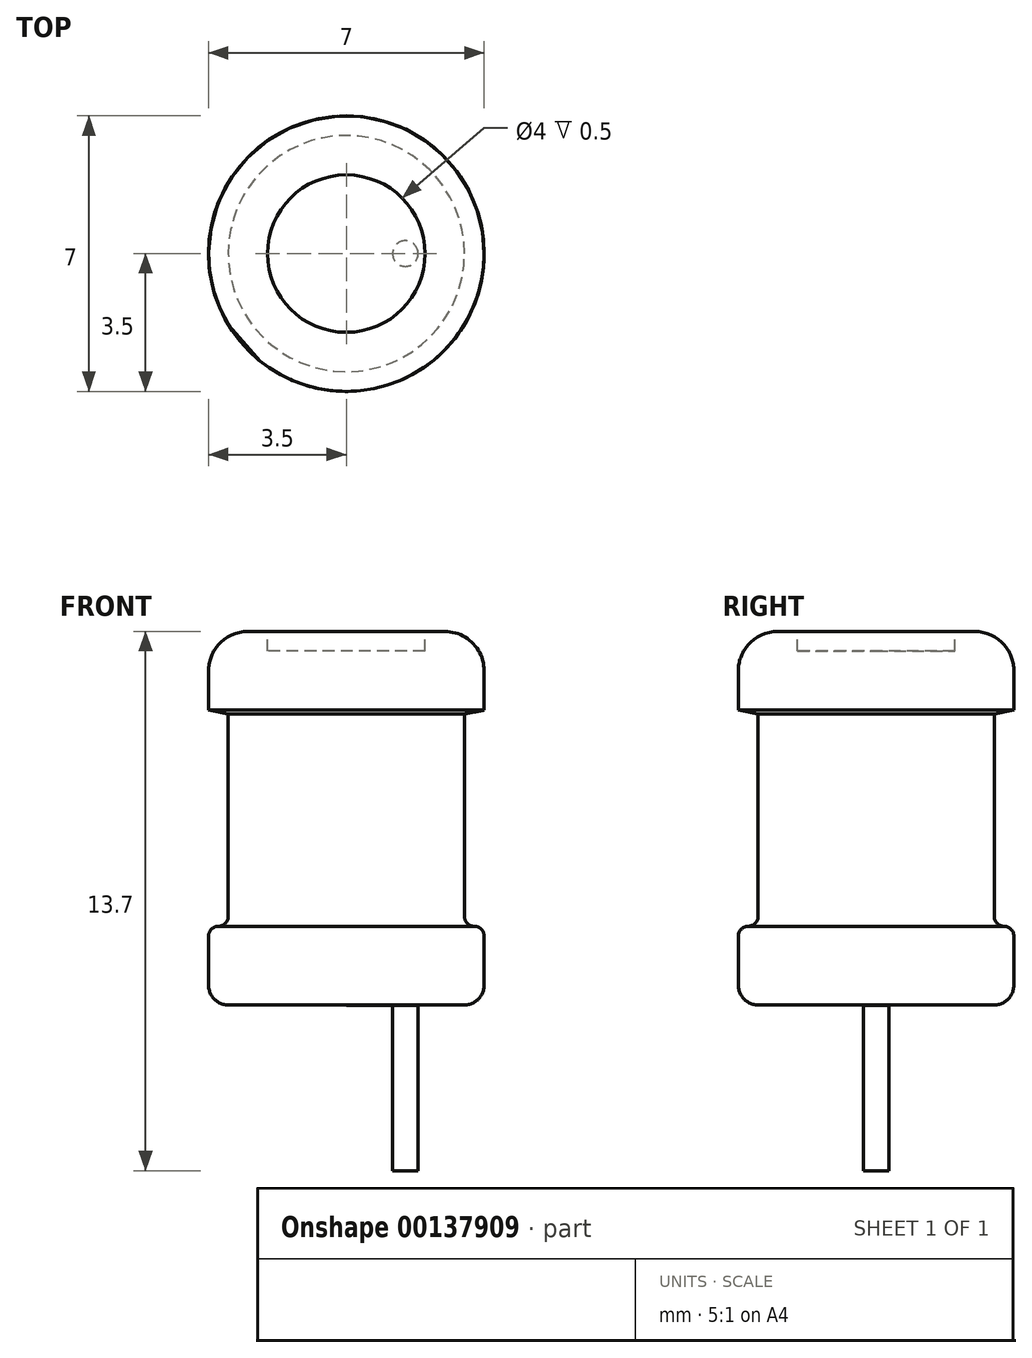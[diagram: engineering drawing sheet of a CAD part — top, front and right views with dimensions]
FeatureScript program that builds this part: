
annotation { "Feature Type Name" : "Feature", "Feature Type Description" : "" }
export const myFeature = defineFeature(function(context is Context, id is Id, definition is map)
    precondition{}
    {
        {
            var Q0;
            Q0=qCreatedBy(makeId("Front.planeOp"),FACE);
            var sketch = newSketch(context, id + "F0", { "sketchPlane" : qUnion([Q0])});
            skLineSegment(sketch, "E0", {"start": v(-2, 9) * mm, "end": v(-2, 9.5) * mm});
            skLineSegment(sketch, "E1", {"start": v(-3.5, 0.5) * mm, "end": v(-3.5, 1.76) * mm});
            skLineSegment(sketch, "E2", {"start": v(-3.25, 2) * mm, "end": v(-3.25, 2) * mm});
            skLineSegment(sketch, "E3", {"start": v(-3, 2.26) * mm, "end": v(-3, 7.4) * mm});
            skLineSegment(sketch, "E4", {"start": v(-3.5, 7.5) * mm, "end": v(-3.5, 8.5) * mm});
            skArc(sketch, "E5.filletArc", {"start": v(-2.5, 9.5) * mm, "mid": v(-3.2, 9.2) * mm, "end": v(-3.5, 8.5) * mm});
            skArc(sketch, "E6.filletArc", {"start": v(-3.25, 2) * mm, "mid": v(-3.43, 1.94) * mm, "end": v(-3.5, 1.76) * mm});
            skArc(sketch, "E7.filletArc", {"start": v(-3.25, 2) * mm, "mid": v(-3.07, 2.08) * mm, "end": v(-3, 2.26) * mm});
            skArc(sketch, "E8.filletArc", {"start": v(-3.5, 0.5) * mm, "mid": v(-3.35, 0.16) * mm, "end": v(-3, 0) * mm});
            skLineSegment(sketch, "E9", {"start": v(-2, 9) * mm, "end": v(0, 9) * mm});
            skLineSegment(sketch, "E10", {"start": v(-3, 0) * mm, "end": v(0, 0) * mm});
            skLineSegment(sketch, "E11", {"start": v(0, 9) * mm, "end": v(0, 0) * mm});
            skLineSegment(sketch, "E12", {"start": v(-2, 9.5) * mm, "end": v(-2.5, 9.5) * mm});
            skLineSegment(sketch, "E13", {"start": v(-3, 7.4) * mm, "end": v(-3.5, 7.5) * mm});
            skSolve(sketch);
        }
        {
            var Q0;
            Q0 = qSketchRegion(id + "F0", true);
            var Q1;
            Q1=sQuery(id+"F0.wireOp",EDGE,"E11");
            revolve(context, id + "F1", {"entities" : qUnion([Q0]), "axis" : qUnion([Q1]), "revolveType" : RevolveType.FULL});
        }
        {
            var Q0;
            Q0=qCreatedBy(makeId("Top.planeOp"),FACE);
            var sketch = newSketch(context, id + "F2", { "sketchPlane" : qUnion([Q0])});
            skLineSegment(sketch, "E14", {"start": v(0, 0) * mm, "end": v(1.5, 0) * mm});
            skCircle(sketch, "E15", {"center": v(1.5, 0) * mm, "radius": 0.33 * mm});
            skCircle(sketch, "E16.MirrorC", {"center": v(-1.5, 0) * mm, "radius": 0.33 * mm});
            skSolve(sketch);
        }
        {
            var Q0;
            Q0=makeQuery(id+"F2.imprint","IMPRINT",FACE,{"disambiguationData":[TD([[makeQuery(id+"F2.imprint","IMPRINT",EDGE,{"derivedFrom":sQuery(id+"F2.wireOp",EDGE,"E15")}),1.0]])]});
            var Q1;
            Q1=makeQuery(id+"F2.imprint","IMPRINT",FACE,{"disambiguationData":[TD([[makeQuery(id+"F2.imprint","IMPRINT",EDGE,{"derivedFrom":sQuery(id+"F2.wireOp",EDGE,"E16.MirrorC")}),-1.0]])]});
            extrude(context, id + "F3", {"entities" : qUnion([Q0, Q1]), "oppositeDirection" : true, "depth" : 4.2 * mm});
        }
    });
